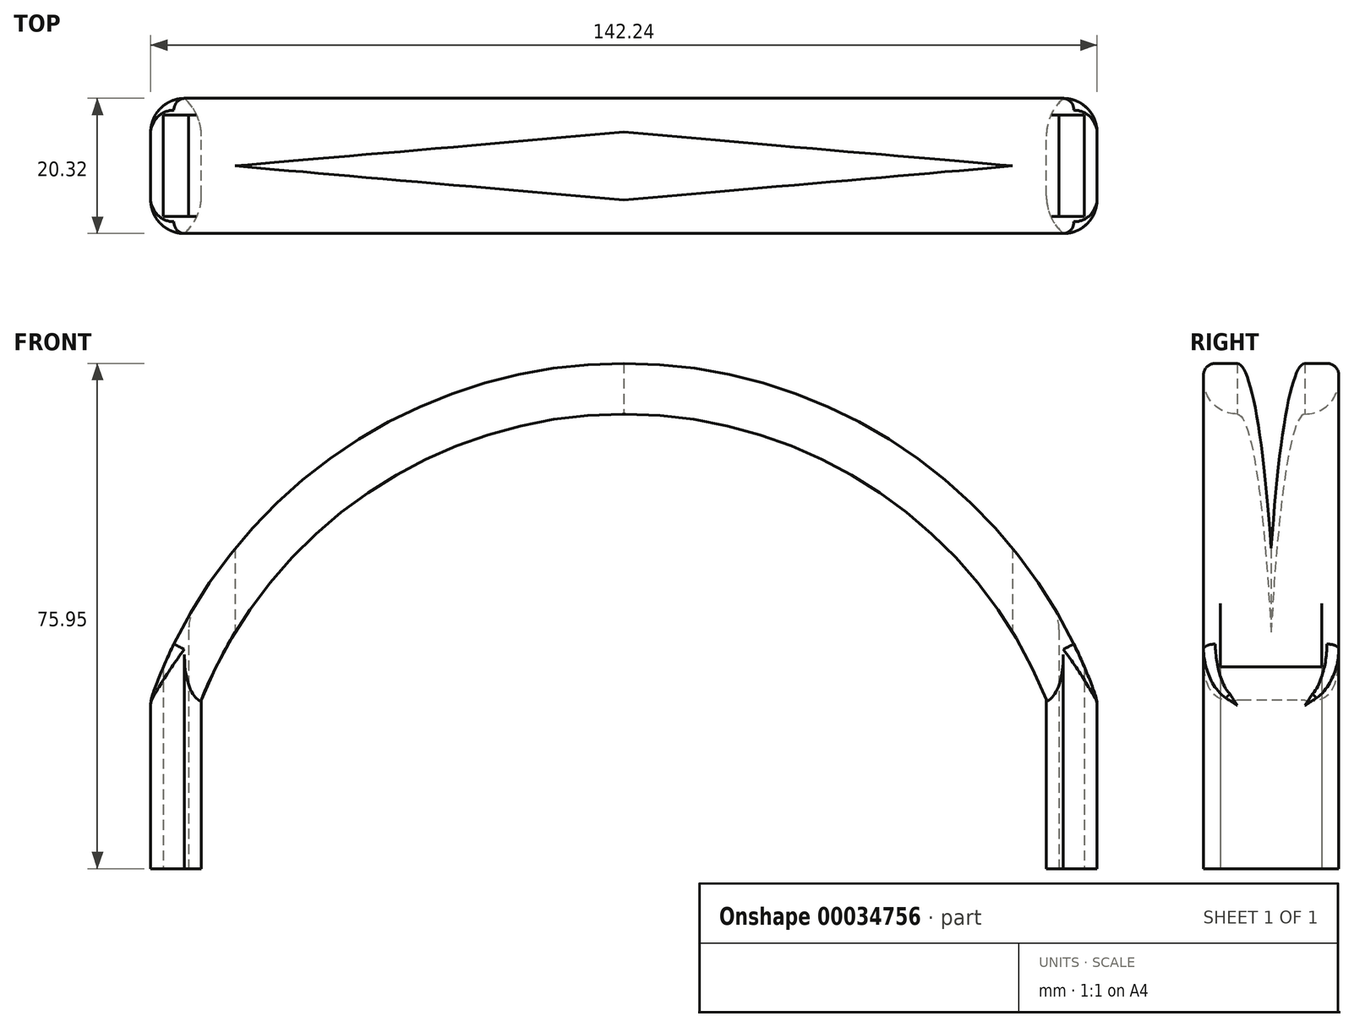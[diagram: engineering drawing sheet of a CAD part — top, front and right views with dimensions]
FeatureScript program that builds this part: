
annotation { "Feature Type Name" : "Feature", "Feature Type Description" : "" }
export const myFeature = defineFeature(function(context is Context, id is Id, definition is map)
    precondition{}
    {
        {
            var Q0;
            Q0=qCreatedBy(makeId("Front.planeOp"),FACE);
            var sketch = newSketch(context, id + "F0", { "sketchPlane" : qUnion([Q0])});
            skLineSegment(sketch, "E0", {"start": v(0, 0) * mm, "end": v(63.5, 0) * mm, "construction": true});
            skLineSegment(sketch, "E1", {"start": v(0, 0) * mm, "end": v(-63.5, 0) * mm, "construction": true});
            skLineSegment(sketch, "E2", {"start": v(-63.5, 0) * mm, "end": v(-63.5, 25.4) * mm});
            skLineSegment(sketch, "E3", {"start": v(63.5, 0) * mm, "end": v(63.5, 25.4) * mm});
            skArc(sketch, "E4", {"start": v(63.5, 25.4) * mm, "mid": v(0, 68.33) * mm, "end": v(-63.5, 25.4) * mm});
            skLineSegment(sketch, "E5", {"start": v(-63.5, 0) * mm, "end": v(-71.12, 0) * mm});
            skLineSegment(sketch, "E6", {"start": v(-71.12, 0) * mm, "end": v(-71.12, 25.4) * mm});
            skLineSegment(sketch, "E7", {"start": v(63.5, 0) * mm, "end": v(71.12, 0) * mm});
            skLineSegment(sketch, "E8", {"start": v(71.12, 0) * mm, "end": v(71.12, 25.4) * mm});
            skPoint(sketch, "E9.endSnap0", {"position": v(0, 68.33) * mm});
            skArc(sketch, "E10", {"start": v(71.12, 25.4) * mm, "mid": v(0, 75.95) * mm, "end": v(-71.12, 25.4) * mm});
            skLineSegment(sketch, "E11", {"start": v(0, 68.33) * mm, "end": v(0, 75.95) * mm, "construction": true});
            skSolve(sketch);
        }
        {
            var Q0;
            Q0 = qSketchRegion(id + "F0", true);
            extrude(context, id + "F1", {"entities" : qUnion([Q0]), "depth" : 20.32 * mm});
        }
        {
            var Q0;
            Q0=qCreatedBy(makeId("Top.planeOp"),FACE);
            var sketch = newSketch(context, id + "F2", { "sketchPlane" : qUnion([Q0])});
            skLineSegment(sketch, "E12", {"start": v(0, -10.16) * mm, "end": v(58.42, -10.16) * mm, "construction": true});
            skLineSegment(sketch, "E13", {"start": v(0, -10.16) * mm, "end": v(-58.42, -10.16) * mm, "construction": true});
            skLineSegment(sketch, "E14", {"start": v(0, -10.16) * mm, "end": v(0, 0) * mm});
            skLineSegment(sketch, "E15", {"start": v(58.42, -10.16) * mm, "end": v(0, -5.08) * mm});
            skLineSegment(sketch, "E16", {"start": v(0, -5.08) * mm, "end": v(-58.42, -10.16) * mm});
            skLineSegment(sketch, "E17", {"start": v(0, -10.16) * mm, "end": v(0, -20.36) * mm, "construction": true});
            skLineSegment(sketch, "E18", {"start": v(58.42, -10.16) * mm, "end": v(0, -15.26) * mm});
            skLineSegment(sketch, "E19", {"start": v(0, -15.26) * mm, "end": v(-58.42, -10.16) * mm});
            skSolve(sketch);
        }
        {
            var Q0;
            Q0 = qSketchRegion(id + "F2", true);
            extrude(context, id + "F3", {"entities" : qUnion([Q0]), "operationType" : NewBodyOperationType.REMOVE, "depth" : 114.64 * mm});
        }
        {
            var Q0;
            Q0=makeQuery(id+"F1.opExtrude","SWEPT_FACE",FACE,{"disambiguationData":[OSD([sQuery(id+"F0.wireOp",EDGE,"E5")])]});
            var sketch = newSketch(context, id + "F4", { "sketchPlane" : qUnion([Q0])});
            skPoint(sketch, "E20.endSnap0", {"position": v(-71.12, 10.16) * mm});
            skLineSegment(sketch, "E21", {"start": v(-69.22, 17.78) * mm, "end": v(-69.22, 2.54) * mm});
            skLineSegment(sketch, "E22", {"start": v(-69.22, 17.78) * mm, "end": v(-65.4, 17.78) * mm});
            skLineSegment(sketch, "E23", {"start": v(-65.4, 17.78) * mm, "end": v(-65.4, 2.54) * mm});
            skLineSegment(sketch, "E24", {"start": v(-65.4, 2.54) * mm, "end": v(-69.22, 2.54) * mm});
            skSolve(sketch);
        }
        {
            var Q0;
            Q0=makeQuery(id+"F1.opExtrude","SWEPT_FACE",FACE,{"disambiguationData":[OSD([sQuery(id+"F0.wireOp",EDGE,"E7")])]});
            var sketch = newSketch(context, id + "F5", { "sketchPlane" : qUnion([Q0])});
            skLineSegment(sketch, "E25", {"start": v(63.5, 20.32) * mm, "end": v(67.31, 20.32) * mm, "construction": true});
            skLineSegment(sketch, "E26", {"start": v(67.31, 20.32) * mm, "end": v(71.12, 20.32) * mm, "construction": true});
            skLineSegment(sketch, "E27", {"start": v(63.5, 15.24) * mm, "end": v(63.5, 20.32) * mm, "construction": true});
            skLineSegment(sketch, "E28", {"start": v(65.4, 17.78) * mm, "end": v(65.4, 2.54) * mm});
            skLineSegment(sketch, "E29", {"start": v(65.4, 2.54) * mm, "end": v(69.22, 2.54) * mm});
            skLineSegment(sketch, "E30", {"start": v(69.22, 2.54) * mm, "end": v(69.22, 17.78) * mm});
            skLineSegment(sketch, "E31", {"start": v(65.4, 17.78) * mm, "end": v(69.22, 17.78) * mm});
            skSolve(sketch);
        }
        {
            var Q0;
            Q0 = qSketchRegion(id + "F5", true);
            extrude(context, id + "F6", {"entities" : qUnion([Q0]), "operationType" : NewBodyOperationType.REMOVE, "oppositeDirection" : true, "depth" : 47.64 * mm});
        }
        {
            var Q0;
            Q0 = qSketchRegion(id + "F4", true);
            extrude(context, id + "F7", {"entities" : qUnion([Q0]), "operationType" : NewBodyOperationType.REMOVE, "oppositeDirection" : true, "depth" : 61.6 * mm});
        }
        {
            var Q0;
            Q0=makeQuery(id+"F1.opExtrude","CAP_EDGE",EDGE,{"disambiguationData":[OSD([sQuery(id+"F0.wireOp",EDGE,"E4")])],"isStart":false});
            var Q1;
            Q1=makeQuery(id+"F1.opExtrude","CAP_EDGE",EDGE,{"disambiguationData":[OSD([sQuery(id+"F0.wireOp",EDGE,"E4")])],"isStart":true});
            fillet(context, id + "F8", {"entities" : qUnion([Q0, Q1]), "radius" : 5.08 * mm, "tangentPropagation" : true, "allowEdgeOverflow" : false});
        }
        {
            var Q0;
            Q0=makeQuery(id+"F1.opExtrude","CAP_EDGE",EDGE,{"disambiguationData":[OSD([sQuery(id+"F0.wireOp",EDGE,"E10")])],"isStart":false});
            var Q1;
            Q1=makeQuery(id+"F1.opExtrude","CAP_EDGE",EDGE,{"disambiguationData":[OSD([sQuery(id+"F0.wireOp",EDGE,"E10")])],"isStart":true});
            fillet(context, id + "F9", {"entities" : qUnion([Q0, Q1]), "radius" : 1.78 * mm, "tangentPropagation" : true, "allowEdgeOverflow" : false});
        }
        {
            var Q0;
            Q0=makeQuery(id+"F1.opExtrude","CAP_EDGE",EDGE,{"disambiguationData":[OSD([sQuery(id+"F0.wireOp",EDGE,"E8")])],"isStart":false});
            var Q1;
            Q1=makeQuery(id+"F1.opExtrude","CAP_EDGE",EDGE,{"disambiguationData":[OSD([sQuery(id+"F0.wireOp",EDGE,"E8")])],"isStart":true});
            var Q2;
            Q2=makeQuery(id+"F1.opExtrude","CAP_EDGE",EDGE,{"disambiguationData":[OSD([sQuery(id+"F0.wireOp",EDGE,"E6")])],"isStart":true});
            var Q3;
            Q3=makeQuery(id+"F1.opExtrude","CAP_EDGE",EDGE,{"disambiguationData":[OSD([sQuery(id+"F0.wireOp",EDGE,"E6")])],"isStart":false});
            fillet(context, id + "F10", {"entities" : qUnion([Q0, Q1, Q2, Q3]), "radius" : 5.08 * mm, "tangentPropagation" : true, "allowEdgeOverflow" : false});
        }
        {
            var Q0;
            Q0=makeQuery(id+"F1.opExtrude","CAP_EDGE",EDGE,{"disambiguationData":[OSD([sQuery(id+"F0.wireOp",EDGE,"E2")])],"isStart":false});
            var Q1;
            Q1=makeQuery(id+"F1.opExtrude","CAP_EDGE",EDGE,{"disambiguationData":[OSD([sQuery(id+"F0.wireOp",EDGE,"E2")])],"isStart":true});
            var Q2;
            Q2=makeQuery(id+"F1.opExtrude","CAP_EDGE",EDGE,{"disambiguationData":[OSD([sQuery(id+"F0.wireOp",EDGE,"E3")])],"isStart":true});
            var Q3;
            Q3=makeQuery(id+"F1.opExtrude","CAP_EDGE",EDGE,{"disambiguationData":[OSD([sQuery(id+"F0.wireOp",EDGE,"E3")])],"isStart":false});
            var Q4;
            Q4=makeQuery(id+"F6.boolean.opBoolean","INTERSECT",EDGE,{"derivedFrom":[makeQuery(id+"F1.opExtrude","SWEPT_FACE",FACE,{"disambiguationData":[OSD([sQuery(id+"F0.wireOp",EDGE,"E10")])]}),makeQuery(id+"F6.opExtrude","SWEPT_FACE",FACE,{"disambiguationData":[OSD([sQuery(id+"F5.wireOp",EDGE,"E28")])]})]});
            var Q5;
            Q5=makeQuery(id+"F7.boolean.opBoolean","INTERSECT",EDGE,{"derivedFrom":[makeQuery(id+"F1.opExtrude","SWEPT_FACE",FACE,{"disambiguationData":[OSD([sQuery(id+"F0.wireOp",EDGE,"E10")])]}),makeQuery(id+"F7.opExtrude","SWEPT_FACE",FACE,{"disambiguationData":[OSD([sQuery(id+"F4.wireOp",EDGE,"E23")])]})]});
            fillet(context, id + "F11", {"entities" : qUnion([Q0, Q1, Q2, Q3, Q4, Q5]), "radius" : 7.62 * mm, "tangentPropagation" : true, "allowEdgeOverflow" : false});
        }
    });
